# Revit family: КШ РАШВОРК  арт.7014 .rfa
name_source: partatom
category: Арматура трубопроводов
units: mm (PartAtom-declared; Revit-internal decimal feet)

## family parameters
Всегда вертикально = Нет
На основе рабочей плоскости = Нет
Общий = Нет
При загрузке вырезать с полостями = Да
Размер круглого соединителя = Использовать диаметр
Тип детали = Нормальный

## types (11) — shared parameters
ADSK_Единица измерения = шт
ADSK_Завод-изготовитель = ООО "ТД "РАШВОРК"
B5 = 28 мм
URL = https://rwru.ru
Изготовитель = ООО "ТД "РАШВОРК"
Корпус = нерж. сталь CF8M
Ручка = нерж. сталь AISI304
Уго_длинна = 115 мм
zero-valued in all types: Отметка по умолчанию

## per-type parameters (varying)
| type | A0 | A00 | A1 | A2 | A3 | A4 | A5 | ADSK_Код изделия | ADSK_Масса | B1 | B2 | B3 | B4 | DN | DN_соединителя | H | L | LL | W | А | Шручки |
| Кран шаровой полнопроходной РАШВОРК 7014-040-63 DN040 PN63, CF8M / AISI316 / PTFE, ВР/ВР, рукоятка-рычаг | 23 мм | 81 мм | 20 мм | 2 мм | 20 мм | 32 мм | 8 мм | 7014-040-63 | 1.3 | 51 мм | 63 мм | 13 мм | 6 мм | 38 мм | 40 мм | 85 мм | 99 мм | 54 мм | 182 мм | 36 мм | 25 мм |
| Кран шаровой полнопроходной РАШВОРК 7014-008-63 DN008 PN63, CF8M / AISI316 / PTFE, ВР/ВР, рукоятка-рычаг | 12 мм | 41 мм | 11 мм | 1 мм | 10 мм | 13 мм | 6 мм | 7014-008-63 | 0.19 | 26 мм | 30 мм | 7 мм | 4 мм | 13 мм | 9 мм | 49 мм | 50 мм | 22 мм | 106 мм | 15 мм | 17 мм |
| Кран шаровой полнопроходной РАШВОРК 7014-010-63 DN010 PN63, CF8M / AISI316 / PTFE, ВР/ВР, рукоятка-рычаг | 12 мм | 41 мм | 11 мм | 1 мм | 10 мм | 13 мм | 6 мм | 7014-010-63 | 0.19 | 26 мм | 30 мм | 7 мм | 4 мм | 13 мм | 10 мм | 49 мм | 50 мм | 22 мм | 106 мм | 15 мм | 17 мм |
| Кран шаровой полнопроходной РАШВОРК 7014-015-63 DN015 PN63, CF8M / AISI316 / PTFE, ВР/ВР, рукоятка-рычаг | 12 мм | 46 мм | 12 мм | 1 мм | 12 мм | 15 мм | 7 мм | 7014-015-63 | 0.26 | 28 мм | 32 мм | 9 мм | 4 мм | 15 мм | 15 мм | 51 мм | 56 мм | 25 мм | 104 мм | 18 мм | 17 мм |
| Кран шаровой полнопроходной РАШВОРК 7014-020-63 DN020 PN63, CF8M / AISI316 / PTFE, ВР/ВР, рукоятка-рычаг | 17 мм | 54 мм | 14 мм | 1 мм | 14 мм | 19 мм | 4 мм | 7014-020-63 | 0.41 | 33 мм | 41 мм | 9 мм | 4 мм | 20 мм | 20 мм | 58 мм | 66 мм | 32 мм | 116 мм | 21 мм | 19 мм |
| Кран шаровой полнопроходной РАШВОРК 7014-025-63 DN025 PN63, CF8M / AISI316 / PTFE, ВР/ВР, рукоятка-рычаг | 21 мм | 64 мм | 15 мм | 1 мм | 19 мм | 23 мм | 3 мм | 7014-025-63 | 0.66 | 38 мм | 46 мм | 10 мм | 5 мм | 25 мм | 25 мм | 73 мм | 79 мм | 39 мм | 148 мм | 25 мм | 22 мм |
| Кран шаровой полнопроходной РАШВОРК 7014-032-63 DN032 PN63, CF8M / AISI316 / PTFE, ВР/ВР, рукоятка-рычаг | 22 мм | 73 мм | 18 мм | 1 мм | 19 мм | 29 мм | 9 мм | 7014-032-63 | 1 | 44 мм | 52 мм | 10 мм | 5 мм | 32 мм | 32 мм | 79 мм | 91 мм | 49 мм | 148 мм | 31 мм | 22 мм |
| Кран шаровой полнопроходной РАШВОРК 7014-050-63 DN050 PN63, CF8M / AISI316 / PTFE, ВР/ВР, рукоятка-рычаг | 28 мм | 99 мм | 22 мм | 2 мм | 29 мм | 39 мм | 10 мм | 7014-050-63 | 2.1 | 61 мм | 73 мм | 13 мм | 6 мм | 50 мм | 50 мм | 95 мм | 121 мм | 67 мм | 182 мм | 45 мм | 25 мм |
| Кран шаровой полнопроходной РАШВОРК 7014-065-63 DN065 PN63, CF8M / AISI316 / PTFE, ВР/ВР, рукоятка-рычаг | 24 мм | 120 мм | 27 мм | 2 мм | 36 мм | 50 мм | 18 мм | 7014-065-63 | 3.83 | 82 мм | 99 мм | 17 мм | 8 мм | 65 мм | 65 мм | 126 мм | 147 мм | 85 мм | 252 мм | 56 мм | 32 мм |
| Кран шаровой полнопроходной РАШВОРК 7014-080-63 DN080 PN63, CF8M / AISI316 / PTFE, ВР/ВР, рукоятка-рычаг | 36 мм | 141 мм | 32 мм | 2 мм | 42 мм | 58 мм | 20 мм | 7014-080-63 | 5.74 | 94 мм | 111 мм | 19 мм | 8 мм | 76 мм | 80 мм | 138 мм | 173 мм | 100 мм | 252 мм | 65 мм | 35 мм |
| Кран шаровой полнопроходной РАШВОРК 7014-100-63 DN100 PN63, CF8M / AISI316 / PTFE, ВР/ВР, рукоятка-рычаг | 46 мм | 180 мм | 35 мм | 2 мм | 54 мм | 74 мм | 25 мм | 7014-100-63 | 10.7 | 114 мм | 131 мм | 24 мм | 8 мм | 94 мм | 100 мм | 158 мм | 222 мм | 128 мм | 283 мм | 84 мм | 32 мм |

note: column(s) folded — value = type name in every type: ADSK_Наименование
